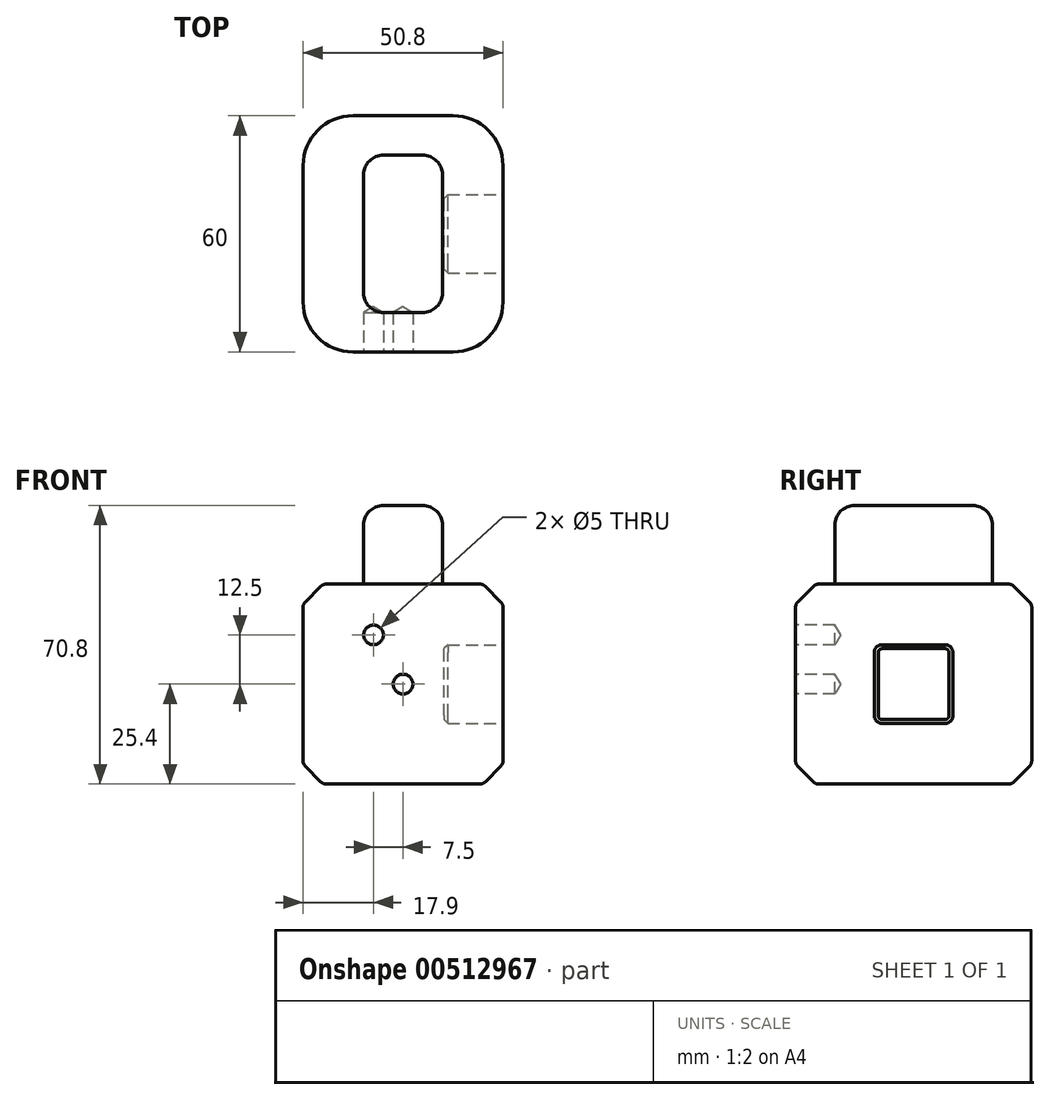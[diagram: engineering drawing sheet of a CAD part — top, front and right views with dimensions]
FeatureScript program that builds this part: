
annotation { "Feature Type Name" : "Feature", "Feature Type Description" : "" }
export const myFeature = defineFeature(function(context is Context, id is Id, definition is map)
    precondition{}
    {
        {
            var Q0;
            Q0=qCreatedBy(makeId("Front.planeOp"),FACE);
            var sketch = newSketch(context, id + "F0", { "sketchPlane" : qUnion([Q0])});
            skLineSegment(sketch, "E0.bottom", {"start": v(-25.4, 25.4) * mm, "end": v(25.4, 25.4) * mm});
            skLineSegment(sketch, "E0.top", {"start": v(-25.4, -25.4) * mm, "end": v(25.4, -25.4) * mm});
            skLineSegment(sketch, "E0.left", {"start": v(-25.4, 25.4) * mm, "end": v(-25.4, -25.4) * mm});
            skLineSegment(sketch, "E0.right", {"start": v(25.4, 25.4) * mm, "end": v(25.4, -25.4) * mm});
            skSolve(sketch);
        }
        {
            var Q0;
            Q0=makeQuery(id+"F0.imprint","IMPRINT",FACE,{"disambiguationData":[TD([[makeQuery(id+"F0.imprint","IMPRINT",EDGE,{"derivedFrom":sQuery(id+"F0.wireOp",EDGE,"E0.bottom")}),-1.0]])]});
            extrude(context, id + "F1", {"entities" : qUnion([Q0]), "endBound" : BoundingType.SYMMETRIC, "depth" : 60 * mm});
        }
        {
            var Q0;
            Q0=makeQuery(id+"F1.opExtrude","CAP_EDGE",EDGE,{"disambiguationData":[OSD([sQuery(id+"F0.wireOp",EDGE,"E0.right")])],"isStart":false});
            var Q1;
            Q1=makeQuery(id+"F1.opExtrude","CAP_EDGE",EDGE,{"disambiguationData":[OSD([sQuery(id+"F0.wireOp",EDGE,"E0.left")])],"isStart":false});
            var Q2;
            Q2=makeQuery(id+"F1.opExtrude","CAP_EDGE",EDGE,{"disambiguationData":[OSD([sQuery(id+"F0.wireOp",EDGE,"E0.right")])],"isStart":true});
            var Q3;
            Q3=makeQuery(id+"F1.opExtrude","CAP_EDGE",EDGE,{"disambiguationData":[OSD([sQuery(id+"F0.wireOp",EDGE,"E0.left")])],"isStart":true});
            fillet(context, id + "F2", {"entities" : qUnion([Q0, Q1, Q2, Q3]), "radius" : 12.7 * mm, "tangentPropagation" : true, "allowEdgeOverflow" : false});
        }
        {
            var Q0;
            Q0=makeQuery(id+"F1.opExtrude","CAP_EDGE",EDGE,{"disambiguationData":[OSD([sQuery(id+"F0.wireOp",EDGE,"E0.bottom")])],"isStart":false});
            var Q1;
            Q1=makeQuery(id+"F1.opExtrude","CAP_EDGE",EDGE,{"disambiguationData":[OSD([sQuery(id+"F0.wireOp",EDGE,"E0.top")])],"isStart":false});
            chamfer(context, id + "F3", {"entities" : qUnion([Q0, Q1]), "width" : 5.08 * mm, "tangentPropagation" : true});
        }
        {
            var Q0;
            Q0=makeQuery(id+"F1.opExtrude","SWEPT_FACE",FACE,{"disambiguationData":[OSD([sQuery(id+"F0.wireOp",EDGE,"E0.bottom")])]});
            var sketch = newSketch(context, id + "F4", { "sketchPlane" : qUnion([Q0])});
            skLineSegment(sketch, "E1.bottom", {"start": v(-5, -20) * mm, "end": v(5, -20) * mm});
            skLineSegment(sketch, "E1.top", {"start": v(-5, 20) * mm, "end": v(5, 20) * mm});
            skLineSegment(sketch, "E1.left", {"start": v(-10, -15) * mm, "end": v(-10, 15) * mm});
            skLineSegment(sketch, "E1.right", {"start": v(10, -15) * mm, "end": v(10, 15) * mm});
            skPoint(sketch, "E2.visualSharp", {"position": v(-10, -20) * mm});
            skArc(sketch, "E2.filletArc", {"start": v(-10, -15) * mm, "mid": v(-8.54, -18.54) * mm, "end": v(-5, -20) * mm});
            skPoint(sketch, "E3.visualSharp", {"position": v(10, -20) * mm});
            skArc(sketch, "E3.filletArc", {"start": v(5, -20) * mm, "mid": v(8.54, -18.54) * mm, "end": v(10, -15) * mm});
            skPoint(sketch, "E4.visualSharp", {"position": v(10, 20) * mm});
            skArc(sketch, "E4.filletArc", {"start": v(10, 15) * mm, "mid": v(8.54, 18.54) * mm, "end": v(5, 20) * mm});
            skPoint(sketch, "E5.visualSharp", {"position": v(-10, 20) * mm});
            skArc(sketch, "E5.filletArc", {"start": v(-5, 20) * mm, "mid": v(-8.54, 18.54) * mm, "end": v(-10, 15) * mm});
            skSolve(sketch);
        }
        {
            var Q0;
            Q0=makeQuery(id+"F4.imprint","IMPRINT",FACE,{"disambiguationData":[TD([[makeQuery(id+"F4.imprint","IMPRINT",EDGE,{"derivedFrom":sQuery(id+"F4.wireOp",EDGE,"E1.bottom")}),1.0]])]});
            extrude(context, id + "F5", {"entities" : qUnion([Q0]), "operationType" : NewBodyOperationType.ADD, "depth" : 20 * mm});
        }
        {
            var Q0;
            Q0=makeQuery(id+"F5.opExtrude","CAP_EDGE",EDGE,{"disambiguationData":[OSD([sQuery(id+"F4.wireOp",EDGE,"E1.right")])],"isStart":false});
            fillet(context, id + "F6", {"entities" : qUnion([Q0]), "radius" : 5 * mm, "tangentPropagation" : true, "allowEdgeOverflow" : false});
        }
        {
            var Q0;
            {var subQ0=sQuery(id+"F0.wireOp",EDGE,"E0.bottom");Q0=makeQuery(id+"F3.opChamfer","BLEND_EDGE",EDGE,{"blendedFrom":[makeQuery(id+"F1.opExtrude","SWEPT_EDGE",EDGE,{"disambiguationData":[OSD([subQ0,sQuery(id+"F0.wireOp",EDGE,"E0.right")])]}),makeQuery(id+"F1.opExtrude","SWEPT_FACE",FACE,{"disambiguationData":[OSD([subQ0])]})],"blendedInto":[makeQuery(id+"F1.opExtrude","SWEPT_FACE",FACE,{"disambiguationData":[OSD([subQ0])]})]});}
            var Q1;
            {var subQ0=sQuery(id+"F0.wireOp",EDGE,"E0.right");Q1=makeQuery(id+"F3.opChamfer","BLEND_EDGE",EDGE,{"blendedFrom":[makeQuery(id+"F1.opExtrude","SWEPT_EDGE",EDGE,{"disambiguationData":[OSD([sQuery(id+"F0.wireOp",EDGE,"E0.bottom"),subQ0])]}),makeQuery(id+"F1.opExtrude","SWEPT_FACE",FACE,{"disambiguationData":[OSD([subQ0])]})],"blendedInto":[makeQuery(id+"F1.opExtrude","SWEPT_FACE",FACE,{"disambiguationData":[OSD([subQ0])]})]});}
            var Q2;
            {var subQ0=sQuery(id+"F0.wireOp",EDGE,"E0.right");Q2=makeQuery(id+"F3.opChamfer","BLEND_EDGE",EDGE,{"blendedFrom":[makeQuery(id+"F1.opExtrude","SWEPT_EDGE",EDGE,{"disambiguationData":[OSD([sQuery(id+"F0.wireOp",EDGE,"E0.top"),subQ0])]}),makeQuery(id+"F1.opExtrude","SWEPT_FACE",FACE,{"disambiguationData":[OSD([subQ0])]})],"blendedInto":[makeQuery(id+"F1.opExtrude","SWEPT_FACE",FACE,{"disambiguationData":[OSD([subQ0])]})]});}
            var Q3;
            {var subQ0=sQuery(id+"F0.wireOp",EDGE,"E0.top");Q3=makeQuery(id+"F3.opChamfer","BLEND_EDGE",EDGE,{"blendedFrom":[makeQuery(id+"F1.opExtrude","SWEPT_EDGE",EDGE,{"disambiguationData":[OSD([subQ0,sQuery(id+"F0.wireOp",EDGE,"E0.right")])]}),makeQuery(id+"F1.opExtrude","SWEPT_FACE",FACE,{"disambiguationData":[OSD([subQ0])]})],"blendedInto":[makeQuery(id+"F1.opExtrude","SWEPT_FACE",FACE,{"disambiguationData":[OSD([subQ0])]})]});}
            fillet(context, id + "F7", {"entities" : qUnion([Q0, Q1, Q2, Q3]), "radius" : 2 * mm, "tangentPropagation" : true, "allowEdgeOverflow" : false});
        }
        {
            var Q0;
            Q0=makeQuery(id+"F1.opExtrude","SWEPT_FACE",FACE,{"disambiguationData":[OSD([sQuery(id+"F0.wireOp",EDGE,"E0.right")])]});
            var sketch = newSketch(context, id + "F8", { "sketchPlane" : qUnion([Q0])});
            skLineSegment(sketch, "E6.bottom", {"start": v(-10, 10) * mm, "end": v(10, 10) * mm});
            skLineSegment(sketch, "E6.top", {"start": v(-10, -10) * mm, "end": v(10, -10) * mm});
            skLineSegment(sketch, "E6.left", {"start": v(-10, 10) * mm, "end": v(-10, -10) * mm});
            skLineSegment(sketch, "E6.right", {"start": v(10, 10) * mm, "end": v(10, -10) * mm});
            skSolve(sketch);
        }
        {
            var Q0;
            Q0 = qSketchRegion(id + "F8", true);
            extrude(context, id + "F9", {"entities" : qUnion([Q0]), "operationType" : NewBodyOperationType.REMOVE, "oppositeDirection" : true, "depth" : 15 * mm});
        }
        {
            var Q0;
            Q0=makeQuery(id+"F9.boolean.opBoolean","COPY",EDGE,{"derivedFrom":makeQuery(id+"F9.opExtrude","SWEPT_EDGE",EDGE,{"disambiguationData":[OSD([sQuery(id+"F8.wireOp",EDGE,"E6.bottom"),sQuery(id+"F8.wireOp",EDGE,"E6.right")])]})});
            var Q1;
            Q1=makeQuery(id+"F9.boolean.opBoolean","COPY",EDGE,{"derivedFrom":makeQuery(id+"F9.opExtrude","SWEPT_EDGE",EDGE,{"disambiguationData":[OSD([sQuery(id+"F8.wireOp",EDGE,"E6.bottom"),sQuery(id+"F8.wireOp",EDGE,"E6.left")])]})});
            var Q2;
            Q2=makeQuery(id+"F9.boolean.opBoolean","COPY",EDGE,{"derivedFrom":makeQuery(id+"F9.opExtrude","SWEPT_EDGE",EDGE,{"disambiguationData":[OSD([sQuery(id+"F8.wireOp",EDGE,"E6.top"),sQuery(id+"F8.wireOp",EDGE,"E6.left")])]})});
            var Q3;
            Q3=makeQuery(id+"F9.boolean.opBoolean","COPY",EDGE,{"derivedFrom":makeQuery(id+"F9.opExtrude","SWEPT_EDGE",EDGE,{"disambiguationData":[OSD([sQuery(id+"F8.wireOp",EDGE,"E6.top"),sQuery(id+"F8.wireOp",EDGE,"E6.right")])]})});
            fillet(context, id + "F10", {"entities" : qUnion([Q0, Q1, Q2, Q3]), "radius" : 2 * mm, "tangentPropagation" : true, "allowEdgeOverflow" : false});
        }
        {
            var Q0;
            Q0=makeQuery(id+"F9.boolean.opBoolean","COPY",EDGE,{"derivedFrom":makeQuery(id+"F9.opExtrude","CAP_EDGE",EDGE,{"disambiguationData":[OSD([sQuery(id+"F8.wireOp",EDGE,"E6.bottom")])],"isStart":false})});
            var Q1;
            Q1=makeQuery(id+"F9.boolean.opBoolean","COPY",EDGE,{"derivedFrom":makeQuery(id+"F9.opExtrude","CAP_EDGE",EDGE,{"disambiguationData":[OSD([sQuery(id+"F8.wireOp",EDGE,"E6.bottom")])],"isStart":true})});
            chamfer(context, id + "F11", {"entities" : qUnion([Q0, Q1]), "width" : 1 * mm, "tangentPropagation" : true});
        }
        {
            var Q0;
            Q0=makeQuery(id+"F1.opExtrude","CAP_FACE",FACE,{"disambiguationData":[OSD([sQuery(id+"F0.wireOp",EDGE,"E0.bottom"),sQuery(id+"F0.wireOp",EDGE,"E0.top"),sQuery(id+"F0.wireOp",EDGE,"E0.left"),sQuery(id+"F0.wireOp",EDGE,"E0.right")])],"isStart":false});
            var sketch = newSketch(context, id + "F12", { "sketchPlane" : qUnion([Q0])});
            skCircle(sketch, "E7", {"center": v(0, 0) * mm, "radius": 6 * mm});
            skSolve(sketch);
        }
        {
            var Q0;
            Q0=sQuery(id+"F12.wireOp",VERTEX,"E7.center");
            var Q1;
            Q1=makeQuery(id+"F1.opExtrude","SWEPT_BODY",BODY,{"disambiguationData":[OSD([sQuery(id+"F0.wireOp",EDGE,"E0.bottom"),sQuery(id+"F0.wireOp",EDGE,"E0.top"),sQuery(id+"F0.wireOp",EDGE,"E0.left"),sQuery(id+"F0.wireOp",EDGE,"E0.right")])]});
            hole(context, id + "F13", {"style" : HoleStyle.SIMPLE, "endStyle" : HoleEndStyle.BLIND, "holeDiameter" : 5 * mm, "holeDepth" : 10 * mm, "isTappedThrough" : true, "tappedDepth" : 12 * mm, "tapClearance" : 3, "locations" : qUnion([Q0]), "scope" : qUnion([Q1])});
        }
        {
            var Q0;
            Q0=makeQuery(id+"F1.opExtrude","CAP_FACE",FACE,{"disambiguationData":[OSD([sQuery(id+"F0.wireOp",EDGE,"E0.bottom"),sQuery(id+"F0.wireOp",EDGE,"E0.top"),sQuery(id+"F0.wireOp",EDGE,"E0.left"),sQuery(id+"F0.wireOp",EDGE,"E0.right")])],"isStart":false});
            var sketch = newSketch(context, id + "F14", { "sketchPlane" : qUnion([Q0])});
            skPoint(sketch, "E8", {"position": v(-7.5, 12.5) * mm});
            skSolve(sketch);
        }
        {
            var Q0;
            Q0=sQuery(id+"F14.wireOp",VERTEX,"E8");
            var Q1;
            Q1=makeQuery(id+"F1.opExtrude","SWEPT_BODY",BODY,{"disambiguationData":[OSD([sQuery(id+"F0.wireOp",EDGE,"E0.bottom"),sQuery(id+"F0.wireOp",EDGE,"E0.top"),sQuery(id+"F0.wireOp",EDGE,"E0.left"),sQuery(id+"F0.wireOp",EDGE,"E0.right")])]});
            hole(context, id + "F15", {"style" : HoleStyle.SIMPLE, "endStyle" : HoleEndStyle.BLIND, "holeDiameter" : 5 * mm, "holeDepth" : 10 * mm, "isTappedThrough" : true, "tappedDepth" : 12 * mm, "tapClearance" : 3, "locations" : qUnion([Q0]), "scope" : qUnion([Q1])});
        }
    });
